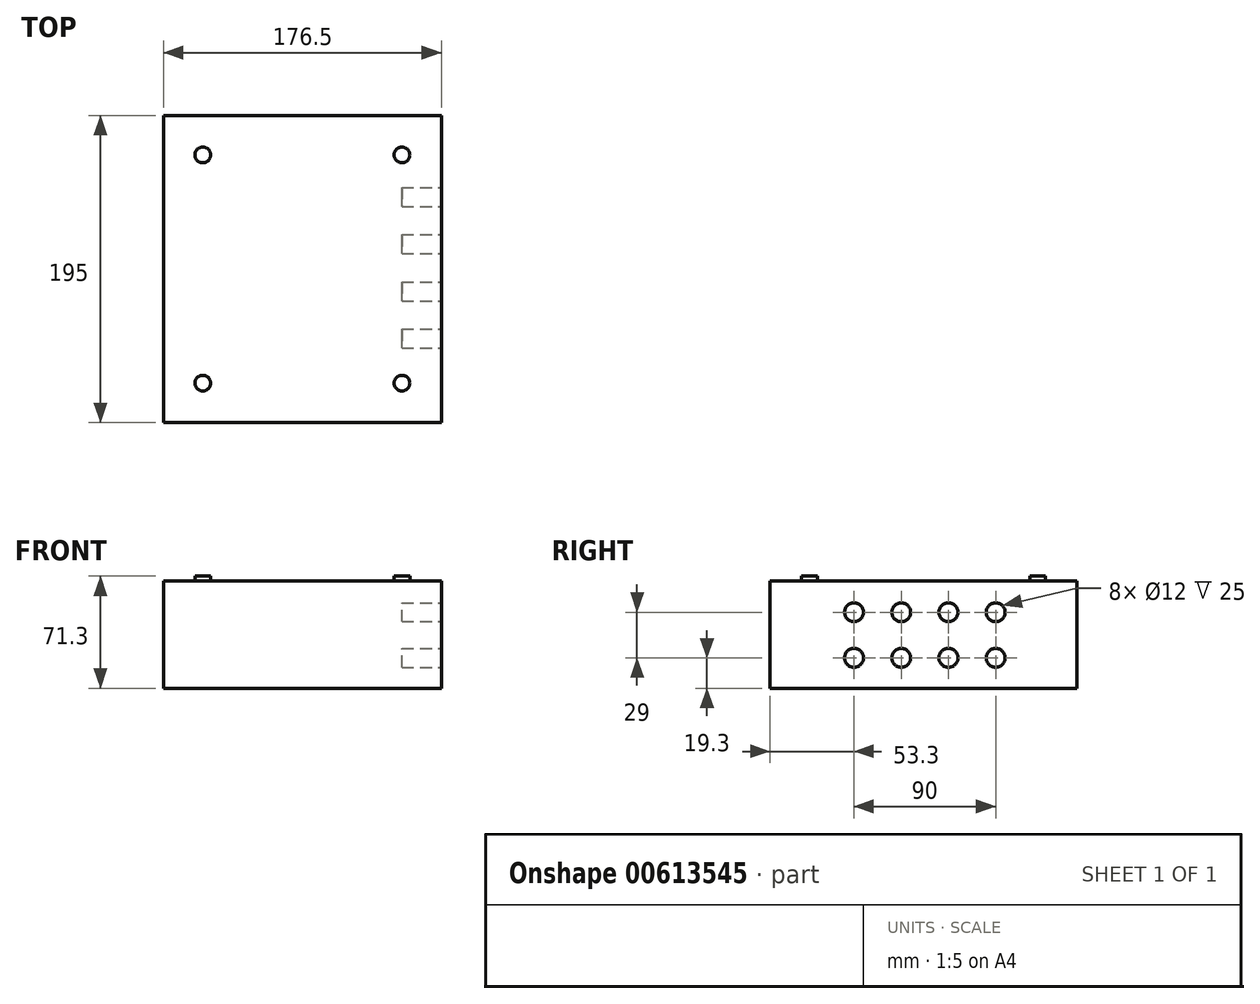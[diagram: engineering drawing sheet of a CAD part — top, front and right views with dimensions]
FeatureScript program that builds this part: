
annotation { "Feature Type Name" : "Feature", "Feature Type Description" : "" }
export const myFeature = defineFeature(function(context is Context, id is Id, definition is map)
    precondition{}
    {
        {
            var Q0;
            Q0=qCreatedBy(makeId("Top.planeOp"),FACE);
            var sketch = newSketch(context, id + "F0", { "sketchPlane" : qUnion([Q0])});
            skLineSegment(sketch, "E0.bottom", {"start": v(0, 0) * mm, "end": v(-176.5, 0) * mm});
            skLineSegment(sketch, "E0.top", {"start": v(0, 195) * mm, "end": v(-176.5, 195) * mm});
            skLineSegment(sketch, "E0.left", {"start": v(0, 0) * mm, "end": v(0, 195) * mm});
            skLineSegment(sketch, "E0.right", {"start": v(-176.5, 0) * mm, "end": v(-176.5, 195) * mm});
            skSolve(sketch);
        }
        {
            var Q0;
            Q0=makeQuery(id+"F0.imprint","IMPRINT",FACE,{"disambiguationData":[TD([[makeQuery(id+"F0.imprint","IMPRINT",EDGE,{"derivedFrom":sQuery(id+"F0.wireOp",EDGE,"E0.bottom")}),-1.0]])]});
            extrude(context, id + "F1", {"entities" : qUnion([Q0]), "oppositeDirection" : true, "depth" : 68.3 * mm, "offsetDistance" : 25 * mm});
        }
        {
            var Q0;
            Q0=makeQuery(id+"F1.opExtrude","CAP_FACE",FACE,{"disambiguationData":[OSD([sQuery(id+"F0.wireOp",EDGE,"E0.bottom"),sQuery(id+"F0.wireOp",EDGE,"E0.top"),sQuery(id+"F0.wireOp",EDGE,"E0.left"),sQuery(id+"F0.wireOp",EDGE,"E0.right")])],"isStart":true});
            var sketch = newSketch(context, id + "F2", { "sketchPlane" : qUnion([Q0])});
            skCircle(sketch, "E1", {"center": v(-151.5, 170) * mm, "radius": 5 * mm});
            skCircle(sketch, "E2", {"center": v(-151.5, 25) * mm, "radius": 5 * mm});
            skCircle(sketch, "E3", {"center": v(-25, 25) * mm, "radius": 5 * mm});
            skCircle(sketch, "E4", {"center": v(-25, 170) * mm, "radius": 5 * mm});
            skSolve(sketch);
        }
        {
            var Q0;
            Q0=makeQuery(id+"F2.imprint","IMPRINT",FACE,{"disambiguationData":[TD([[makeQuery(id+"F2.imprint","IMPRINT",EDGE,{"derivedFrom":sQuery(id+"F2.wireOp",EDGE,"E4")}),1.0]])]});
            var Q1;
            Q1=makeQuery(id+"F2.imprint","IMPRINT",FACE,{"disambiguationData":[TD([[makeQuery(id+"F2.imprint","IMPRINT",EDGE,{"derivedFrom":sQuery(id+"F2.wireOp",EDGE,"E1")}),1.0]])]});
            var Q2;
            Q2=makeQuery(id+"F2.imprint","IMPRINT",FACE,{"disambiguationData":[TD([[makeQuery(id+"F2.imprint","IMPRINT",EDGE,{"derivedFrom":sQuery(id+"F2.wireOp",EDGE,"E2")}),1.0]])]});
            var Q3;
            Q3=makeQuery(id+"F2.imprint","IMPRINT",FACE,{"disambiguationData":[TD([[makeQuery(id+"F2.imprint","IMPRINT",EDGE,{"derivedFrom":sQuery(id+"F2.wireOp",EDGE,"E3")}),1.0]])]});
            extrude(context, id + "F3", {"entities" : qUnion([Q0, Q1, Q2, Q3]), "operationType" : NewBodyOperationType.ADD, "depth" : 3 * mm, "offsetDistance" : 25 * mm});
        }
        {
            var Q0;
            Q0=makeQuery(id+"F1.opExtrude","SWEPT_FACE",FACE,{"disambiguationData":[OSD([sQuery(id+"F0.wireOp",EDGE,"E0.left")])]});
            var sketch = newSketch(context, id + "F4", { "sketchPlane" : qUnion([Q0])});
            skCircle(sketch, "E5", {"center": v(143.3, -20) * mm, "radius": 6 * mm});
            skCircle(sketch, "E6.0.1.0", {"center": v(143.3, -49) * mm, "radius": 6 * mm});
            skCircle(sketch, "E6.1.0.0", {"center": v(113.3, -20) * mm, "radius": 6 * mm});
            skCircle(sketch, "E6.1.1.0", {"center": v(113.3, -49) * mm, "radius": 6 * mm});
            skCircle(sketch, "E6.2.0.0", {"center": v(83.3, -20) * mm, "radius": 6 * mm});
            skCircle(sketch, "E6.2.1.0", {"center": v(83.3, -49) * mm, "radius": 6 * mm});
            skCircle(sketch, "E6.3.0.0", {"center": v(53.3, -20) * mm, "radius": 6 * mm});
            skCircle(sketch, "E6.3.1.0", {"center": v(53.3, -49) * mm, "radius": 6 * mm});
            skLineSegment(sketch, "E6.direction1", {"start": v(143.3, -20) * mm, "end": v(113.3, -20) * mm, "construction": true});
            skLineSegment(sketch, "E6.direction2", {"start": v(143.3, -20) * mm, "end": v(143.3, -49) * mm, "construction": true});
            skSolve(sketch);
        }
        {
            var Q0;
            Q0=makeQuery(id+"F4.imprint","IMPRINT",FACE,{"disambiguationData":[TD([[makeQuery(id+"F4.imprint","IMPRINT",EDGE,{"derivedFrom":sQuery(id+"F4.wireOp",EDGE,"E6.0.1.0")}),1.0]])]});
            var Q1;
            Q1=makeQuery(id+"F4.imprint","IMPRINT",FACE,{"disambiguationData":[TD([[makeQuery(id+"F4.imprint","IMPRINT",EDGE,{"derivedFrom":sQuery(id+"F4.wireOp",EDGE,"E6.1.1.0")}),1.0]])]});
            var Q2;
            Q2=makeQuery(id+"F4.imprint","IMPRINT",FACE,{"disambiguationData":[TD([[makeQuery(id+"F4.imprint","IMPRINT",EDGE,{"derivedFrom":sQuery(id+"F4.wireOp",EDGE,"E6.2.1.0")}),1.0]])]});
            var Q3;
            Q3=makeQuery(id+"F4.imprint","IMPRINT",FACE,{"disambiguationData":[TD([[makeQuery(id+"F4.imprint","IMPRINT",EDGE,{"derivedFrom":sQuery(id+"F4.wireOp",EDGE,"E6.3.1.0")}),1.0]])]});
            var Q4;
            Q4=makeQuery(id+"F4.imprint","IMPRINT",FACE,{"disambiguationData":[TD([[makeQuery(id+"F4.imprint","IMPRINT",EDGE,{"derivedFrom":sQuery(id+"F4.wireOp",EDGE,"E6.3.0.0")}),1.0]])]});
            var Q5;
            Q5=makeQuery(id+"F4.imprint","IMPRINT",FACE,{"disambiguationData":[TD([[makeQuery(id+"F4.imprint","IMPRINT",EDGE,{"derivedFrom":sQuery(id+"F4.wireOp",EDGE,"E6.2.0.0")}),1.0]])]});
            var Q6;
            Q6=makeQuery(id+"F4.imprint","IMPRINT",FACE,{"disambiguationData":[TD([[makeQuery(id+"F4.imprint","IMPRINT",EDGE,{"derivedFrom":sQuery(id+"F4.wireOp",EDGE,"E6.1.0.0")}),1.0]])]});
            var Q7;
            Q7=makeQuery(id+"F4.imprint","IMPRINT",FACE,{"disambiguationData":[TD([[makeQuery(id+"F4.imprint","IMPRINT",EDGE,{"derivedFrom":sQuery(id+"F4.wireOp",EDGE,"E5")}),1.0]])]});
            extrude(context, id + "F5", {"entities" : qUnion([Q0, Q1, Q2, Q3, Q4, Q5, Q6, Q7]), "operationType" : NewBodyOperationType.REMOVE, "oppositeDirection" : true, "depth" : 25 * mm, "offsetDistance" : 25 * mm});
        }
    });
